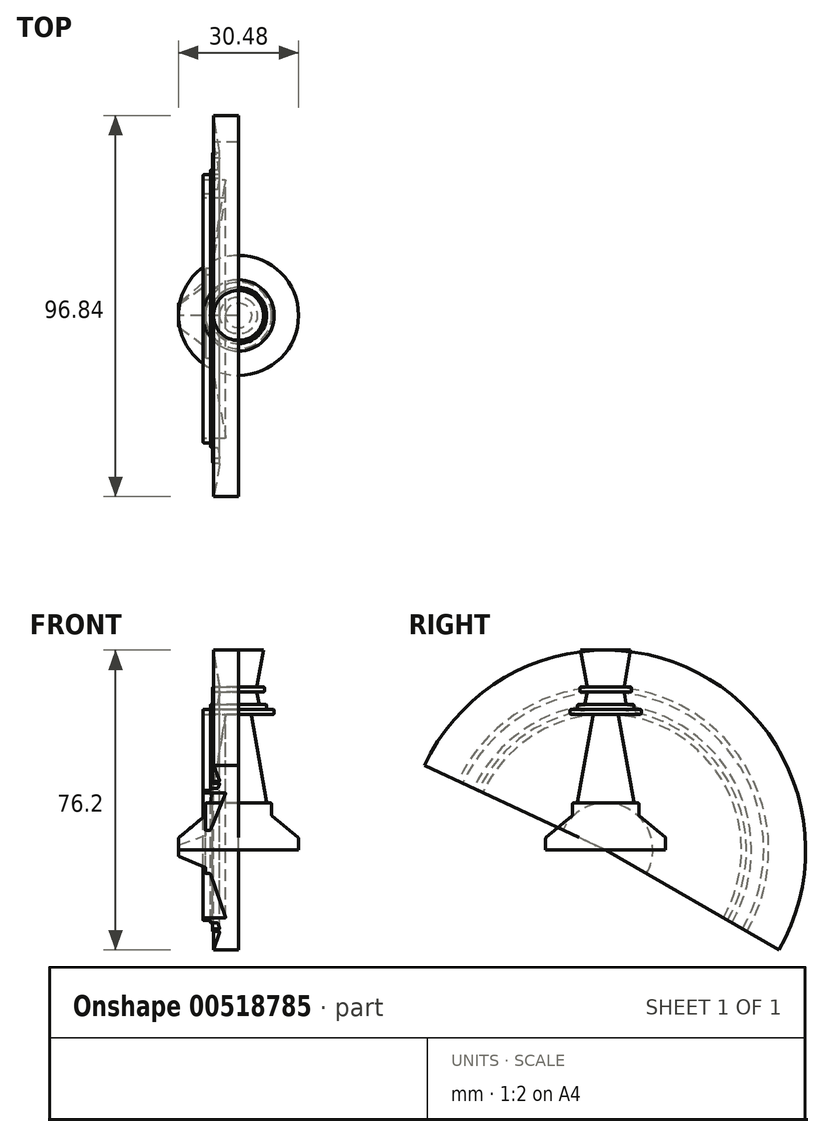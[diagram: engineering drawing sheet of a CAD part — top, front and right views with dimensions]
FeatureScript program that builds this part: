
annotation { "Feature Type Name" : "Feature", "Feature Type Description" : "" }
export const myFeature = defineFeature(function(context is Context, id is Id, definition is map)
    precondition{}
    {
        {
            var Q0;
            Q0=qCreatedBy(makeId("Front.planeOp"),FACE);
            var sketch = newSketch(context, id + "F0", { "sketchPlane" : qUnion([Q0])});
            skLineSegment(sketch, "E0.bottom", {"start": v(0, 0) * mm, "end": v(-15.24, 0) * mm});
            skLineSegment(sketch, "E0.top", {"start": v(0, 50.8) * mm, "end": v(-6.35, 50.8) * mm});
            skLineSegment(sketch, "E0.left", {"start": v(0, 0) * mm, "end": v(0, 50.8) * mm});
            skLineSegment(sketch, "E1", {"start": v(-15.24, 0) * mm, "end": v(-15.24, 2.93) * mm});
            skLineSegment(sketch, "E2", {"start": v(-15.13, 3.18) * mm, "end": v(-8.54, 8.7) * mm});
            skLineSegment(sketch, "E3", {"start": v(-8.43, 8.94) * mm, "end": v(-8.43, 11.65) * mm});
            skLineSegment(sketch, "E4", {"start": v(-8.11, 11.97) * mm, "end": v(-7.43, 11.97) * mm});
            skLineSegment(sketch, "E5", {"start": v(-7.11, 12.23) * mm, "end": v(-3.26, 34.11) * mm});
            skLineSegment(sketch, "E6", {"start": v(-3.57, 34.48) * mm, "end": v(-8.74, 34.48) * mm});
            skLineSegment(sketch, "E7", {"start": v(-9.06, 34.8) * mm, "end": v(-9.06, 35.44) * mm});
            skLineSegment(sketch, "E8", {"start": v(-8.74, 35.75) * mm, "end": v(-7.47, 35.75) * mm});
            skLineSegment(sketch, "E9", {"start": v(-7.15, 36.07) * mm, "end": v(-7.15, 36.7) * mm});
            skLineSegment(sketch, "E10", {"start": v(-6.83, 37.02) * mm, "end": v(-5.51, 37.02) * mm});
            skLineSegment(sketch, "E11", {"start": v(-5.2, 37.29) * mm, "end": v(-4.76, 39.78) * mm});
            skLineSegment(sketch, "E12", {"start": v(-5.07, 40.15) * mm, "end": v(-6.28, 40.15) * mm});
            skLineSegment(sketch, "E13", {"start": v(-6.6, 40.47) * mm, "end": v(-6.6, 41.1) * mm});
            skLineSegment(sketch, "E14", {"start": v(-6.28, 41.42) * mm, "end": v(-5.07, 41.42) * mm});
            skLineSegment(sketch, "E15", {"start": v(-4.76, 41.8) * mm, "end": v(-6.35, 50.8) * mm});
            skPoint(sketch, "E16.visualSharp", {"position": v(-15.24, 3.08) * mm});
            skArc(sketch, "E16.filletArc", {"start": v(-15.13, 3.18) * mm, "mid": v(-15.21, 3.07) * mm, "end": v(-15.24, 2.93) * mm});
            skPoint(sketch, "E17.visualSharp", {"position": v(-8.43, 8.8) * mm});
            skArc(sketch, "E17.filletArc", {"start": v(-8.54, 8.7) * mm, "mid": v(-8.46, 8.8) * mm, "end": v(-8.43, 8.94) * mm});
            skPoint(sketch, "E18.visualSharp", {"position": v(-3.2, 34.48) * mm});
            skArc(sketch, "E18.filletArc", {"start": v(-3.26, 34.11) * mm, "mid": v(-3.33, 34.37) * mm, "end": v(-3.57, 34.48) * mm});
            skPoint(sketch, "E19.visualSharp", {"position": v(-8.43, 11.97) * mm});
            skArc(sketch, "E19.filletArc", {"start": v(-8.11, 11.97) * mm, "mid": v(-8.34, 11.88) * mm, "end": v(-8.43, 11.65) * mm});
            skPoint(sketch, "E20.visualSharp", {"position": v(-7.16, 11.97) * mm});
            skArc(sketch, "E20.filletArc", {"start": v(-7.43, 11.97) * mm, "mid": v(-7.22, 12.04) * mm, "end": v(-7.11, 12.23) * mm});
            skPoint(sketch, "E21.visualSharp", {"position": v(-9.06, 34.48) * mm});
            skArc(sketch, "E21.filletArc", {"start": v(-9.06, 34.8) * mm, "mid": v(-8.96, 34.58) * mm, "end": v(-8.74, 34.48) * mm});
            skPoint(sketch, "E22.visualSharp", {"position": v(-9.06, 35.75) * mm});
            skArc(sketch, "E22.filletArc", {"start": v(-8.74, 35.75) * mm, "mid": v(-8.96, 35.66) * mm, "end": v(-9.06, 35.44) * mm});
            skPoint(sketch, "E23.visualSharp", {"position": v(-7.15, 35.75) * mm});
            skArc(sketch, "E23.filletArc", {"start": v(-7.47, 35.75) * mm, "mid": v(-7.25, 35.85) * mm, "end": v(-7.15, 36.07) * mm});
            skPoint(sketch, "E24.visualSharp", {"position": v(-7.15, 37.02) * mm});
            skArc(sketch, "E24.filletArc", {"start": v(-6.83, 37.02) * mm, "mid": v(-7.06, 36.93) * mm, "end": v(-7.15, 36.7) * mm});
            skPoint(sketch, "E25.visualSharp", {"position": v(-5.25, 37.02) * mm});
            skArc(sketch, "E25.filletArc", {"start": v(-5.51, 37.02) * mm, "mid": v(-5.3, 37.1) * mm, "end": v(-5.2, 37.29) * mm});
            skPoint(sketch, "E26.visualSharp", {"position": v(-4.7, 40.15) * mm});
            skArc(sketch, "E26.filletArc", {"start": v(-4.76, 39.78) * mm, "mid": v(-4.83, 40.04) * mm, "end": v(-5.07, 40.15) * mm});
            skPoint(sketch, "E27.visualSharp", {"position": v(-6.6, 40.15) * mm});
            skArc(sketch, "E27.filletArc", {"start": v(-6.6, 40.47) * mm, "mid": v(-6.5, 40.24) * mm, "end": v(-6.28, 40.15) * mm});
            skPoint(sketch, "E28.visualSharp", {"position": v(-6.6, 41.42) * mm});
            skArc(sketch, "E28.filletArc", {"start": v(-6.28, 41.42) * mm, "mid": v(-6.5, 41.33) * mm, "end": v(-6.6, 41.1) * mm});
            skPoint(sketch, "E29.visualSharp", {"position": v(-4.7, 41.42) * mm});
            skArc(sketch, "E29.filletArc", {"start": v(-5.07, 41.42) * mm, "mid": v(-4.83, 41.53) * mm, "end": v(-4.76, 41.8) * mm});
            skSolve(sketch);
        }
        {
            var Q0;
            Q0=makeQuery(id+"F0.imprint","IMPRINT",FACE,{"disambiguationData":[TD([[makeQuery(id+"F0.imprint","IMPRINT",EDGE,{"derivedFrom":sQuery(id+"F0.wireOp",EDGE,"E0.bottom")}),-1.0]])]});
            var Q1;
            Q1=sQuery(id+"F0.wireOp",EDGE,"E0.bottom");
            revolve(context, id + "F1", {"entities" : qUnion([Q0]), "axis" : qUnion([Q1]), "revolveType" : RevolveType.TWO_DIRECTIONS, "angle" : 120 * degree, "angleBack" : 295 * degree});
        }
        {
            var Q0;
            Q0=makeQuery(id+"F0.imprint","IMPRINT",FACE,{"disambiguationData":[TD([[makeQuery(id+"F0.imprint","IMPRINT",EDGE,{"derivedFrom":sQuery(id+"F0.wireOp",EDGE,"E0.bottom")}),-1.0]])]});
            var Q1;
            Q1=sQuery(id+"F0.wireOp",EDGE,"E0.left");
            revolve(context, id + "F2", {"entities" : qUnion([Q0]), "axis" : qUnion([Q1]), "revolveType" : RevolveType.FULL});
        }
    });
